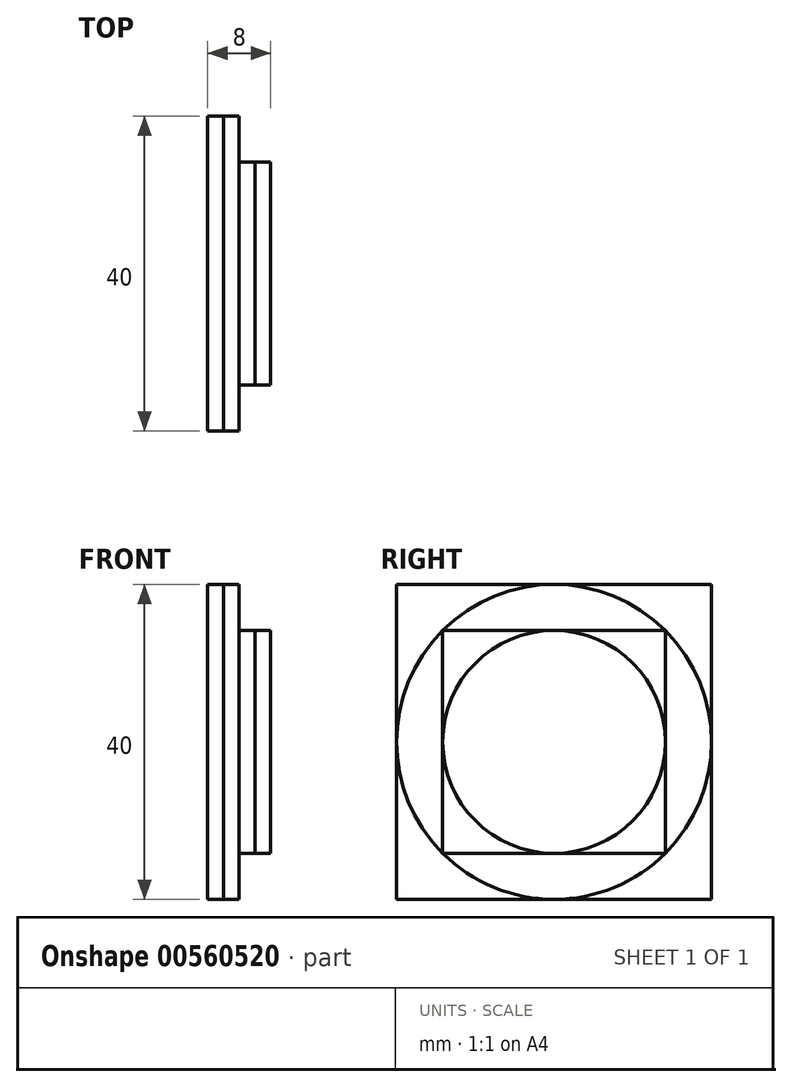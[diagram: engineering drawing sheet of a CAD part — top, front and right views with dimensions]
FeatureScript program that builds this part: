
annotation { "Feature Type Name" : "Feature", "Feature Type Description" : "" }
export const myFeature = defineFeature(function(context is Context, id is Id, definition is map)
    precondition{}
    {
        {
            var Q0;
            Q0=qCreatedBy(makeId("Front.planeOp"),FACE);
            var sketch = newSketch(context, id + "F0", { "sketchPlane" : qUnion([Q0])});
            skLineSegment(sketch, "E0.bottom", {"start": v(-62, 20) * mm, "end": v(-60, 20) * mm});
            skLineSegment(sketch, "E0.top", {"start": v(-62, -20) * mm, "end": v(-60, -20) * mm});
            skLineSegment(sketch, "E0.left", {"start": v(-62, 20) * mm, "end": v(-62, -20) * mm});
            skLineSegment(sketch, "E0.right", {"start": v(-60, 20) * mm, "end": v(-60, -20) * mm});
            skSolve(sketch);
        }
        {
            var Q0;
            Q0 = qSketchRegion(id + "F0", true);
            extrude(context, id + "F1", {"entities" : qUnion([Q0]), "endBound" : BoundingType.SYMMETRIC, "depth" : 40 * mm, "offsetDistance" : 25 * mm});
        }
        {
            var Q0;
            Q0=qCreatedBy(makeId("Front.planeOp"),FACE);
            var sketch = newSketch(context, id + "F2", { "sketchPlane" : qUnion([Q0])});
            skLineSegment(sketch, "E1.bottom", {"start": v(-60, 20) * mm, "end": v(-58, 20) * mm});
            skLineSegment(sketch, "E1.left", {"start": v(-60, 20) * mm, "end": v(-60, 0) * mm});
            skLineSegment(sketch, "E1.right", {"start": v(-58, 20) * mm, "end": v(-58, 0) * mm});
            skLineSegment(sketch, "E2", {"start": v(0, 0) * mm, "end": v(-120, 0) * mm, "construction": true});
            skPoint(sketch, "E2.endSnap0", {"position": v(-58, 0) * mm});
            skLineSegment(sketch, "E3", {"start": v(-58, 0) * mm, "end": v(-60, 0) * mm});
            skPoint(sketch, "E4.orphan", {"position": v(-58, -20) * mm});
            skPoint(sketch, "E5.orphan", {"position": v(-60, -20) * mm});
            skSolve(sketch);
        }
        {
            var Q0;
            Q0=makeQuery(id+"F2.imprint","IMPRINT",FACE,{"disambiguationData":[TD([[makeQuery(id+"F2.imprint","IMPRINT",EDGE,{"derivedFrom":sQuery(id+"F2.wireOp",EDGE,"E1.bottom")}),-1.0]])]});
            var Q1;
            Q1=sQuery(id+"F2.wireOp",EDGE,"E2");
            revolve(context, id + "F3", {"operationType" : NewBodyOperationType.ADD, "entities" : qUnion([Q0]), "axis" : qUnion([Q1]), "revolveType" : RevolveType.FULL});
        }
        {
            var Q0;
            Q0=qCreatedBy(makeId("Right.planeOp"),FACE);
            cPlane(context, id + "F4", {"entities" : qUnion([Q0]), "cplaneType" : CPlaneType.OFFSET, "offset" : 58 * mm, "oppositeDirection" : true, "width" : 150 * mm, "height" : 150 * mm});
        }
        {
            var Q0;
            Q0=qCreatedBy(id+"F4.planeOp",FACE);
            var sketch = newSketch(context, id + "F5", { "sketchPlane" : qUnion([Q0])});
            skPoint(sketch, "E6.0", {"position": v(20, 20) * mm});
            skPoint(sketch, "E7.0", {"position": v(-20, -20) * mm});
            skPoint(sketch, "E8", {"position": v(14.14, 14.14) * mm});
            skLineSegment(sketch, "E9.bottom", {"start": v(14.14, 14.14) * mm, "end": v(-14.14, 14.14) * mm});
            skLineSegment(sketch, "E9.top", {"start": v(14.14, -14.14) * mm, "end": v(-14.14, -14.14) * mm});
            skLineSegment(sketch, "E9.left", {"start": v(14.14, 14.14) * mm, "end": v(14.14, -14.14) * mm});
            skLineSegment(sketch, "E9.right", {"start": v(-14.14, 14.14) * mm, "end": v(-14.14, -14.14) * mm});
            skPoint(sketch, "E9.middle", {"position": v(0, 0) * mm});
            skSolve(sketch);
        }
        {
            var Q0;
            Q0=makeQuery(id+"F5.imprint","IMPRINT",FACE,{"disambiguationData":[TD([[makeQuery(id+"F5.imprint","IMPRINT",EDGE,{"derivedFrom":sQuery(id+"F5.wireOp",EDGE,"E9.bottom")}),1.0]])]});
            extrude(context, id + "F6", {"entities" : qUnion([Q0]), "operationType" : NewBodyOperationType.ADD, "depth" : 2 * mm, "offsetDistance" : 25 * mm});
        }
        {
            var Q0;
            Q0=qCreatedBy(makeId("Front.planeOp"),FACE);
            var sketch = newSketch(context, id + "F7", { "sketchPlane" : qUnion([Q0])});
            skPoint(sketch, "E10.0", {"position": v(-56, 14.14) * mm});
            skLineSegment(sketch, "E11.bottom", {"start": v(-54, 0) * mm, "end": v(-56, 0) * mm});
            skLineSegment(sketch, "E11.top", {"start": v(-54, 14.14) * mm, "end": v(-56, 14.14) * mm});
            skLineSegment(sketch, "E11.left", {"start": v(-54, 0) * mm, "end": v(-54, 14.14) * mm});
            skLineSegment(sketch, "E11.right", {"start": v(-56, 0) * mm, "end": v(-56, 14.14) * mm});
            skSolve(sketch);
        }
        {
            var Q0;
            Q0=makeQuery(id+"F7.imprint","IMPRINT",FACE,{"disambiguationData":[TD([[makeQuery(id+"F7.imprint","IMPRINT",EDGE,{"derivedFrom":sQuery(id+"F7.wireOp",EDGE,"E11.bottom")}),-1.0]])]});
            var Q1;
            Q1=sQuery(id+"F7.wireOp",EDGE,"E11.bottom");
            revolve(context, id + "F8", {"operationType" : NewBodyOperationType.ADD, "entities" : qUnion([Q0]), "axis" : qUnion([Q1]), "revolveType" : RevolveType.FULL});
        }
    });
